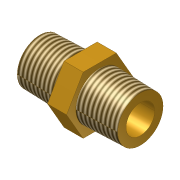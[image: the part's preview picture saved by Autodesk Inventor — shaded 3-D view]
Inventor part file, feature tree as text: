
AUTODESK INVENTOR PART (.ipt)
format: ipt  version: Autodesk Inventor 10  size: 179,712 bytes
history: native  units: mm (DEFAULTED — no unit token found)
features: thread x4, sketch x1, imported_body x1
ambient origin geometry x8: Origin, YZ Plane, XZ Plane, XY Plane, X Axis, Y Axis, Z Axis, Center Point
feature tree (6):
  sketch  "Sketch1"
  imported_body  "Base1"
  thread  "Thread1"  [1 undecoded]
  thread  "Thread2"  [1 undecoded]
  thread  "Thread3"  [1 undecoded]
  thread  "Thread4"  [1 undecoded]
note: 4 required parameter values undecoded (feature->parameter linkage not recoverable at this tier; creation-order binding heuristic only, values carry confidence <= 0.55)
